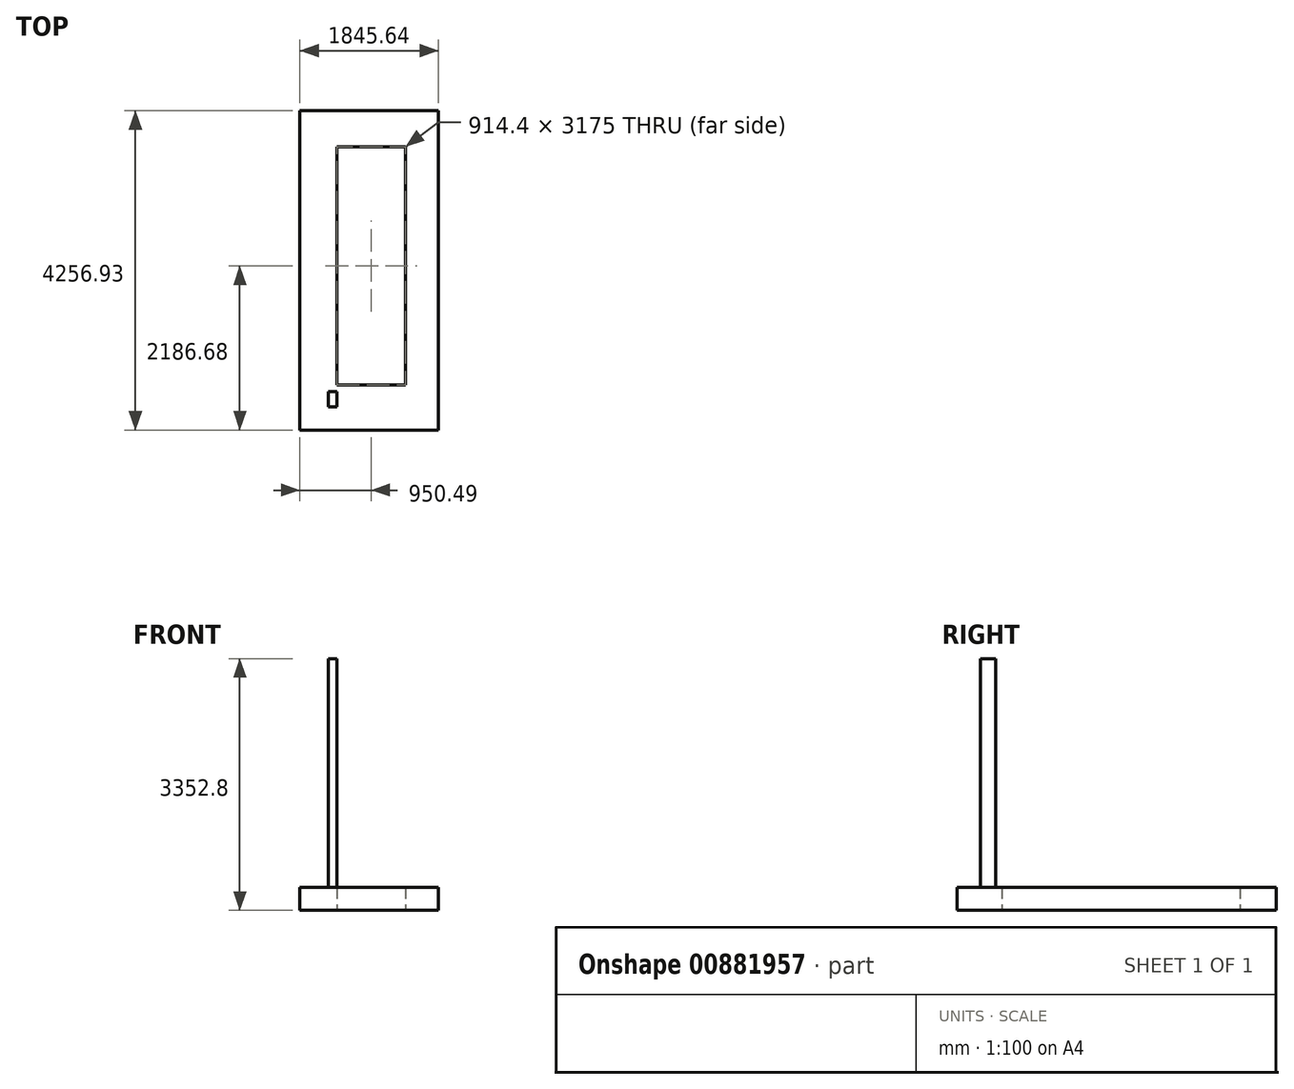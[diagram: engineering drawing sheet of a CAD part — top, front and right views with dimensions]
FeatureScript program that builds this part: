
annotation { "Feature Type Name" : "Feature", "Feature Type Description" : "" }
export const myFeature = defineFeature(function(context is Context, id is Id, definition is map)
    precondition{}
    {
        {
            var Q0;
            Q0=qCreatedBy(makeId("Top.planeOp"),FACE);
            var sketch = newSketch(context, id + "F0", { "sketchPlane" : qUnion([Q0])});
            skLineSegment(sketch, "E0.bottom", {"start": v(0, 86.63) * mm, "end": v(914.4, 86.63) * mm});
            skLineSegment(sketch, "E0.top", {"start": v(0, 3261.63) * mm, "end": v(914.4, 3261.63) * mm});
            skLineSegment(sketch, "E0.left", {"start": v(0, 86.63) * mm, "end": v(0, 3261.63) * mm});
            skLineSegment(sketch, "E0.right", {"start": v(914.4, 86.63) * mm, "end": v(914.4, 3261.63) * mm});
            skLineSegment(sketch, "E1.bottom", {"start": v(-493.3, -512.55) * mm, "end": v(1352.35, -512.55) * mm});
            skLineSegment(sketch, "E1.top", {"start": v(-493.3, 3744.38) * mm, "end": v(1352.35, 3744.38) * mm});
            skLineSegment(sketch, "E1.left", {"start": v(-493.3, -512.55) * mm, "end": v(-493.3, 3744.38) * mm});
            skLineSegment(sketch, "E1.right", {"start": v(1352.35, -512.55) * mm, "end": v(1352.35, 3744.38) * mm});
            skSolve(sketch);
        }
        {
            var Q0;
            Q0 = qSketchRegion(id + "F0", true);
            extrude(context, id + "F1", {"entities" : qUnion([Q0]), "depth" : 304.8 * mm, "offsetDistance" : 25.4 * mm});
        }
        {
            var Q0;
            Q0=makeQuery(id+"F1.opExtrude","CAP_FACE",FACE,{"disambiguationData":[OSD([sQuery(id+"F0.wireOp",EDGE,"E0.bottom"),sQuery(id+"F0.wireOp",EDGE,"E0.top"),sQuery(id+"F0.wireOp",EDGE,"E0.left"),sQuery(id+"F0.wireOp",EDGE,"E0.right"),sQuery(id+"F0.wireOp",EDGE,"E1.bottom"),sQuery(id+"F0.wireOp",EDGE,"E1.top"),sQuery(id+"F0.wireOp",EDGE,"E1.left"),sQuery(id+"F0.wireOp",EDGE,"E1.right")])],"isStart":false});
            var sketch = newSketch(context, id + "F2", { "sketchPlane" : qUnion([Q0])});
            skLineSegment(sketch, "E2.bottom", {"start": v(-114.3, 0) * mm, "end": v(0, 0) * mm});
            skLineSegment(sketch, "E2.top", {"start": v(-114.3, -203.2) * mm, "end": v(0, -203.2) * mm});
            skLineSegment(sketch, "E2.left", {"start": v(-114.3, 0) * mm, "end": v(-114.3, -203.2) * mm});
            skLineSegment(sketch, "E2.right", {"start": v(0, 0) * mm, "end": v(0, -203.2) * mm});
            skSolve(sketch);
        }
        {
            var Q0;
            Q0=makeQuery(id+"F2.imprint","IMPRINT",FACE,{"disambiguationData":[TD([[makeQuery(id+"F2.imprint","IMPRINT",EDGE,{"derivedFrom":sQuery(id+"F2.wireOp",EDGE,"E2.bottom")}),-1.0]])]});
            extrude(context, id + "F3", {"entities" : qUnion([Q0]), "operationType" : NewBodyOperationType.ADD, "depth" : 3048 * mm, "offsetDistance" : 25.4 * mm});
        }
    });
